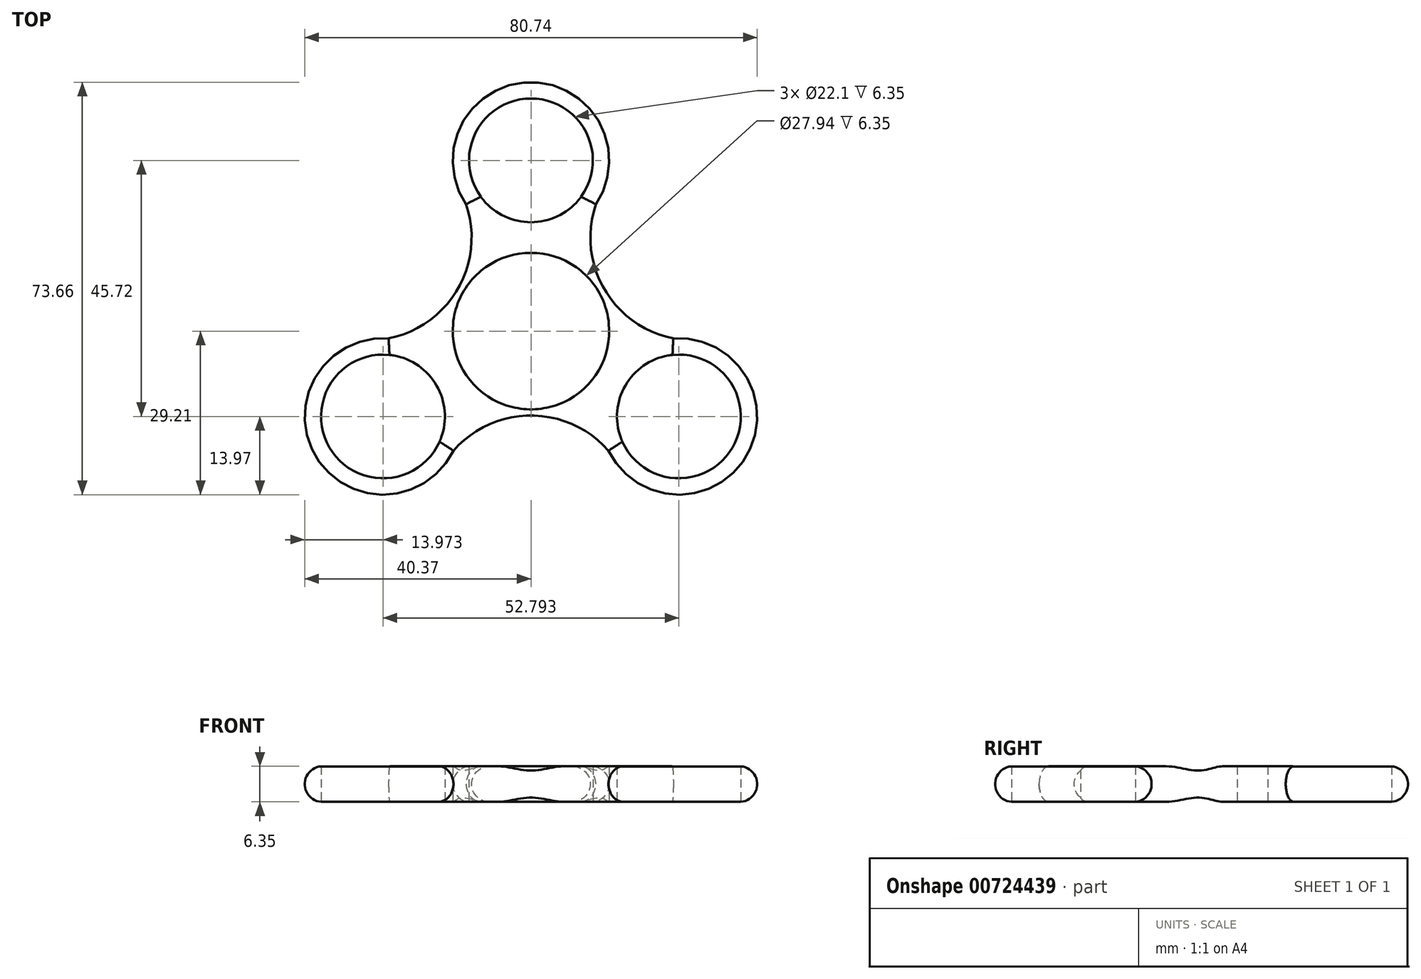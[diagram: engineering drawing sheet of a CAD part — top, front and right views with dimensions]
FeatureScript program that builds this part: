
annotation { "Feature Type Name" : "Feature", "Feature Type Description" : "" }
export const myFeature = defineFeature(function(context is Context, id is Id, definition is map)
    precondition{}
    {
        {
            var Q0;
            Q0=qCreatedBy(makeId("Top.planeOp"),FACE);
            var sketch = newSketch(context, id + "F0", { "sketchPlane" : qUnion([Q0])});
            skCircle(sketch, "E0", {"center": v(0, 0) * mm, "radius": 11.05 * mm});
            skCircle(sketch, "E1", {"center": v(0, 0) * mm, "radius": 13.97 * mm});
            skLineSegment(sketch, "E2", {"start": v(0, 0) * mm, "end": v(0, 30.48) * mm});
            skCircle(sketch, "E3", {"center": v(0, 30.48) * mm, "radius": 11.05 * mm});
            skCircle(sketch, "E4", {"center": v(0, 30.48) * mm, "radius": 13.97 * mm});
            skCircle(sketch, "E5.1.0", {"center": v(-26.4, -15.24) * mm, "radius": 11.05 * mm});
            skCircle(sketch, "E5.1.1", {"center": v(-26.4, -15.24) * mm, "radius": 13.97 * mm});
            skCircle(sketch, "E5.2.0", {"center": v(26.4, -15.24) * mm, "radius": 11.05 * mm});
            skCircle(sketch, "E5.2.1", {"center": v(26.4, -15.24) * mm, "radius": 13.97 * mm});
            skLineSegment(sketch, "E6", {"start": v(0, 0) * mm, "end": v(-13.06, 7.54) * mm});
            skArc(sketch, "E7", {"start": v(-29.62, -1.65) * mm, "mid": v(-13.06, 7.54) * mm, "end": v(-13.38, 26.48) * mm});
            skPoint(sketch, "E8.orphan", {"position": v(-57.98, 33.48) * mm});
            skArc(sketch, "E9.1.0", {"start": v(16.24, -24.83) * mm, "mid": v(0, -15.08) * mm, "end": v(-16.24, -24.83) * mm});
            skArc(sketch, "E9.2.0", {"start": v(13.38, 26.48) * mm, "mid": v(13.06, 7.54) * mm, "end": v(29.62, -1.65) * mm});
            skSolve(sketch);
        }
        {
            var Q0;
            Q0 = qSketchRegion(id + "F0", true);
            extrude(context, id + "F1", {"entities" : qUnion([Q0]), "depth" : 6.35 * mm, "offsetDistance" : 25.4 * mm});
        }
        {
            var Q0;
            Q0=makeQuery(id+"F1.opExtrude","CAP_EDGE",EDGE,{"disambiguationData":[OSD([sQuery(id+"F0.wireOp",EDGE,"E4")])],"isStart":false});
            var Q1;
            Q1=makeQuery(id+"F1.opExtrude","CAP_EDGE",EDGE,{"disambiguationData":[OSD([sQuery(id+"F0.wireOp",EDGE,"E7")])],"isStart":false});
            var Q2;
            Q2=makeQuery(id+"F1.opExtrude","CAP_EDGE",EDGE,{"disambiguationData":[OSD([sQuery(id+"F0.wireOp",EDGE,"E5.1.1")])],"isStart":false});
            var Q3;
            Q3=makeQuery(id+"F1.opExtrude","CAP_EDGE",EDGE,{"disambiguationData":[OSD([sQuery(id+"F0.wireOp",EDGE,"E9.1.0")])],"isStart":false});
            var Q4;
            Q4=makeQuery(id+"F1.opExtrude","CAP_EDGE",EDGE,{"disambiguationData":[OSD([sQuery(id+"F0.wireOp",EDGE,"E5.2.1")])],"isStart":false});
            var Q5;
            Q5=makeQuery(id+"F1.opExtrude","CAP_EDGE",EDGE,{"disambiguationData":[OSD([sQuery(id+"F0.wireOp",EDGE,"E9.2.0")])],"isStart":false});
            var Q6;
            Q6=makeQuery(id+"F1.opExtrude","CAP_EDGE",EDGE,{"disambiguationData":[OSD([sQuery(id+"F0.wireOp",EDGE,"E5.2.1")])],"isStart":true});
            var Q7;
            Q7=makeQuery(id+"F1.opExtrude","CAP_EDGE",EDGE,{"disambiguationData":[OSD([sQuery(id+"F0.wireOp",EDGE,"E4")])],"isStart":true});
            var Q8;
            Q8=makeQuery(id+"F1.opExtrude","CAP_EDGE",EDGE,{"disambiguationData":[OSD([sQuery(id+"F0.wireOp",EDGE,"E9.2.0")])],"isStart":true});
            var Q9;
            Q9=makeQuery(id+"F1.opExtrude","CAP_EDGE",EDGE,{"disambiguationData":[OSD([sQuery(id+"F0.wireOp",EDGE,"E7")])],"isStart":true});
            var Q10;
            Q10=makeQuery(id+"F1.opExtrude","CAP_EDGE",EDGE,{"disambiguationData":[OSD([sQuery(id+"F0.wireOp",EDGE,"E5.1.1")])],"isStart":true});
            var Q11;
            Q11=makeQuery(id+"F1.opExtrude","CAP_EDGE",EDGE,{"disambiguationData":[OSD([sQuery(id+"F0.wireOp",EDGE,"E9.1.0")])],"isStart":true});
            fillet(context, id + "F2", {"entities" : qUnion([Q0, Q1, Q2, Q3, Q4, Q5, Q6, Q7, Q8, Q9, Q10, Q11]), "radius" : 3.17 * mm, "tangentPropagation" : true, "allowEdgeOverflow" : false});
        }
    });
